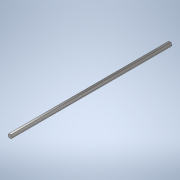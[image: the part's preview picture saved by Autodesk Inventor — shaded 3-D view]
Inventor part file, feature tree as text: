
AUTODESK INVENTOR PART (.ipt)
format: ipt  version: 2020 (Build 240168000, 168)  size: 105,984 bytes
history: native  units: in
note: dims shown in document units (in); Inventor stores cm internally (conversion verified against a paired STEP export)
features: extrude x1, sketch x1
ambient origin geometry x8: Origin, YZ Plane, XZ Plane, XY Plane, X Axis, Y Axis, Z Axis, Center Point
bodies: Solid1 (feature_tree)
feature tree (2):
  extrude  "Extrusion1"  Depth=22.0in TaperAngle=0.0deg
  sketch  "Sketch1"  dims[d0=0.5in d1=22.0in d2=0.0in]
